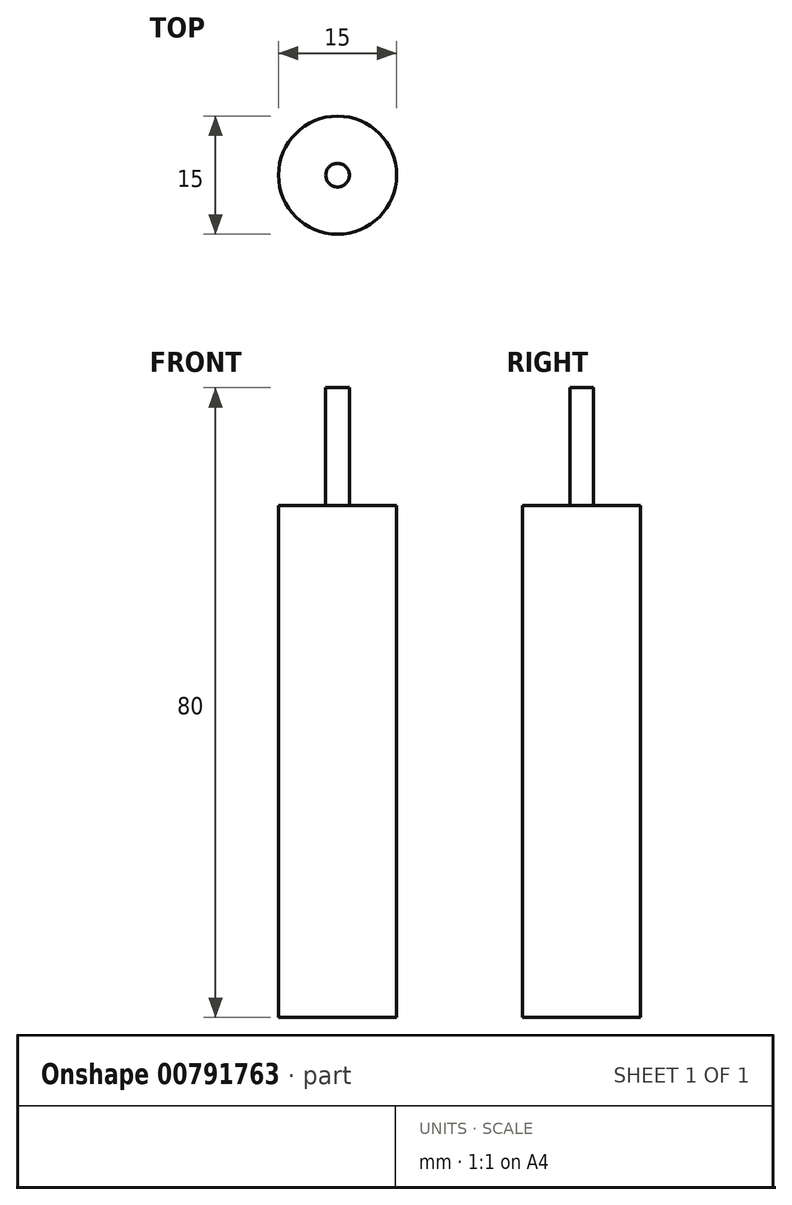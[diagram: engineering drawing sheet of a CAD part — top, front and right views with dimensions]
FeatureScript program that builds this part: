
annotation { "Feature Type Name" : "Feature", "Feature Type Description" : "" }
export const myFeature = defineFeature(function(context is Context, id is Id, definition is map)
    precondition{}
    {
        {
            var Q0;
            Q0=qCreatedBy(makeId("Top.planeOp"),FACE);
            var sketch = newSketch(context, id + "F0", { "sketchPlane" : qUnion([Q0])});
            skCircle(sketch, "E0", {"center": v(0, 0) * mm, "radius": 7.5 * mm});
            skSolve(sketch);
        }
        {
            var Q0;
            Q0 = qSketchRegion(id + "F0", true);
            extrude(context, id + "F1", {"entities" : qUnion([Q0]), "endBound" : BoundingType.SYMMETRIC, "depth" : 65 * mm, "offsetDistance" : 25 * mm});
        }
        {
            var Q0;
            Q0=makeQuery(id+"F1.opExtrude","CAP_FACE",FACE,{"disambiguationData":[OSD([sQuery(id+"F0.wireOp",EDGE,"E0")])],"isStart":false});
            var sketch = newSketch(context, id + "F2", { "sketchPlane" : qUnion([Q0])});
            skCircle(sketch, "E1", {"center": v(0, 0) * mm, "radius": 1.5 * mm});
            skSolve(sketch);
        }
        {
            var Q0;
            Q0 = qSketchRegion(id + "F2", true);
            extrude(context, id + "F3", {"entities" : qUnion([Q0]), "operationType" : NewBodyOperationType.ADD, "depth" : 15 * mm, "offsetDistance" : 25 * mm});
        }
    });
